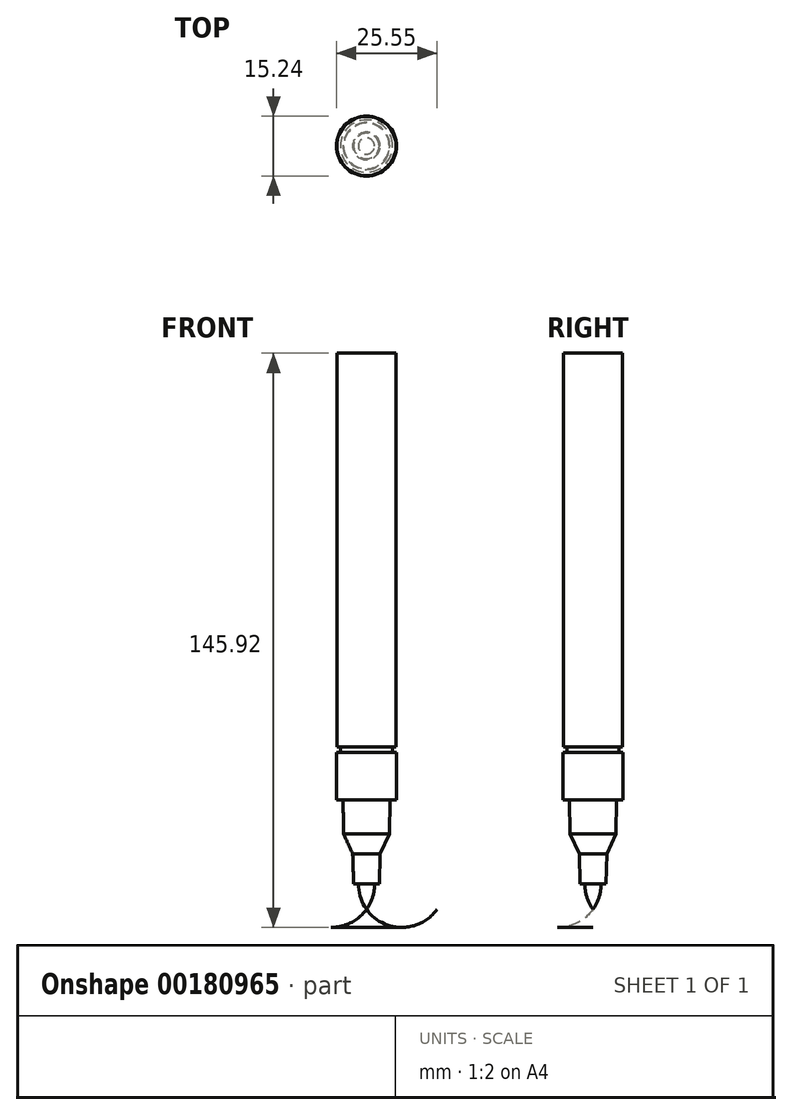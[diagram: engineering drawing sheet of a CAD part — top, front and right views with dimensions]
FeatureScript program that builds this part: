
annotation { "Feature Type Name" : "Feature", "Feature Type Description" : "" }
export const myFeature = defineFeature(function(context is Context, id is Id, definition is map)
    precondition{}
    {
        {
            var Q0;
            Q0=qCreatedBy(makeId("Top.planeOp"),FACE);
            var sketch = newSketch(context, id + "F0", { "sketchPlane" : qUnion([Q0])});
            skCircle(sketch, "E0", {"center": v(0, 0) * mm, "radius": 7.5 * mm});
            skSolve(sketch);
        }
        {
            var Q0;
            Q0=qSketchRegion(id+"F0",true);
            extrude(context, id + "F1", {"entities" : qUnion([Q0]), "depth" : 100 * mm});
        }
        {
            var Q0;
            Q0=makeQuery(id+"F1.opExtrude","CAP_FACE",FACE,{"disambiguationData":[OSD([sQuery(id+"F0.wireOp",EDGE,"E0")])],"isStart":true});
            var sketch = newSketch(context, id + "F2", { "sketchPlane" : qUnion([Q0])});
            skCircle(sketch, "E1", {"center": v(0, 0) * mm, "radius": 6.65 * mm});
            skSolve(sketch);
        }
        {
            var Q0;
            Q0=qSketchRegion(id+"F2",true);
            extrude(context, id + "F3", {"entities" : qUnion([Q0]), "operationType" : NewBodyOperationType.ADD, "depth" : 1.5 * mm});
        }
        {
            var Q0;
            Q0=makeQuery(id+"F3.opExtrude","CAP_FACE",FACE,{"disambiguationData":[OSD([sQuery(id+"F2.wireOp",EDGE,"E1")])],"isStart":false});
            var sketch = newSketch(context, id + "F4", { "sketchPlane" : qUnion([Q0])});
            skCircle(sketch, "E2", {"center": v(0, 0) * mm, "radius": 7.62 * mm});
            skSolve(sketch);
        }
        {
            var Q0;
            Q0=qSketchRegion(id+"F4",true);
            extrude(context, id + "F5", {"entities" : qUnion([Q0]), "operationType" : NewBodyOperationType.ADD, "depth" : 12 * mm});
        }
        {
            var Q0;
            Q0=makeQuery(id+"F5.opExtrude","CAP_FACE",FACE,{"disambiguationData":[OSD([sQuery(id+"F4.wireOp",EDGE,"E2")])],"isStart":false});
            var sketch = newSketch(context, id + "F6", { "sketchPlane" : qUnion([Q0])});
            skCircle(sketch, "E3", {"center": v(0, 0) * mm, "radius": 5.95 * mm});
            skSolve(sketch);
        }
        {
            var Q0;
            Q0=makeQuery(id+"F6.imprint","IMPRINT",FACE,{"disambiguationData":[TD([[makeQuery(id+"F6.imprint","IMPRINT",EDGE,{"derivedFrom":sQuery(id+"F6.wireOp",EDGE,"E3")}),1.0]])]});
            cPlane(context, id + "F7", {"entities" : qUnion([Q0]), "cplaneType" : CPlaneType.OFFSET, "offset" : 8.7 * mm, "width" : 150 * mm, "height" : 150 * mm});
        }
        {
            var Q0;
            Q0=qCreatedBy(id+"F7.planeOp",FACE);
            var sketch = newSketch(context, id + "F8", { "sketchPlane" : qUnion([Q0])});
            skCircle(sketch, "E4", {"center": v(0, 0) * mm, "radius": 5.8 * mm});
            skSolve(sketch);
        }
        {
            var Q1;
            Q1=makeQuery(id+"F6.imprint","IMPRINT",FACE,{"disambiguationData":[TD([[makeQuery(id+"F6.imprint","IMPRINT",EDGE,{"derivedFrom":sQuery(id+"F6.wireOp",EDGE,"E3")}),1.0]])]});
            var Q2;
            Q2=makeQuery(id+"F8.imprint","IMPRINT",FACE,{"disambiguationData":[TD([[makeQuery(id+"F8.imprint","IMPRINT",EDGE,{"derivedFrom":sQuery(id+"F8.wireOp",EDGE,"E4")}),1.0]])]});
            loft(context, id + "F9", {"operationType" : NewBodyOperationType.ADD, "sheetProfilesArray" : [{ "sheetProfileEntities" : qUnion([Q1]) }, { "sheetProfileEntities" : qUnion([Q2]) }]});
        }
        {
            var Q0;
            Q0=qCreatedBy(id+"F7.planeOp",FACE);
            cPlane(context, id + "F10", {"entities" : qUnion([Q0]), "cplaneType" : CPlaneType.OFFSET, "offset" : 5 * mm, "width" : 150 * mm, "height" : 150 * mm});
        }
        {
            var Q0;
            Q0=qCreatedBy(id+"F10.planeOp",FACE);
            var sketch = newSketch(context, id + "F11", { "sketchPlane" : qUnion([Q0])});
            skCircle(sketch, "E5", {"center": v(0, 0) * mm, "radius": 3.5 * mm});
            skSolve(sketch);
        }
        {
            var Q1;
            Q1=makeQuery(id+"F9.opLoft","CAP_FACE",FACE,{"disambiguationData":[OSD([makeQuery(id+"F8.imprint","IMPRINT",FACE,{"disambiguationData":[TD([[makeQuery(id+"F8.imprint","IMPRINT",EDGE,{"derivedFrom":sQuery(id+"F8.wireOp",EDGE,"E4")}),1.0]])]})])],"isStart":true});
            var Q2;
            Q2=makeQuery(id+"F11.imprint","IMPRINT",FACE,{"disambiguationData":[TD([[makeQuery(id+"F11.imprint","IMPRINT",EDGE,{"derivedFrom":sQuery(id+"F11.wireOp",EDGE,"E5")}),1.0]])]});
            loft(context, id + "F12", {"operationType" : NewBodyOperationType.ADD, "sheetProfilesArray" : [{ "sheetProfileEntities" : qUnion([Q1]) }, { "sheetProfileEntities" : qUnion([Q2]) }]});
        }
        {
            var Q0;
            Q0=qCreatedBy(id+"F10.planeOp",FACE);
            cPlane(context, id + "F13", {"entities" : qUnion([Q0]), "cplaneType" : CPlaneType.OFFSET, "offset" : 7.7 * mm, "width" : 150 * mm, "height" : 150 * mm});
        }
        {
            var Q0;
            Q0=qCreatedBy(id+"F13.planeOp",FACE);
            var sketch = newSketch(context, id + "F14", { "sketchPlane" : qUnion([Q0])});
            skCircle(sketch, "E6", {"center": v(0, 0) * mm, "radius": 3.25 * mm});
            skSolve(sketch);
        }
        {
            var Q1;
            Q1=makeQuery(id+"F12.opLoft","CAP_FACE",FACE,{"disambiguationData":[OSD([makeQuery(id+"F11.imprint","IMPRINT",FACE,{"disambiguationData":[TD([[makeQuery(id+"F11.imprint","IMPRINT",EDGE,{"derivedFrom":sQuery(id+"F11.wireOp",EDGE,"E5")}),1.0]])]})])],"isStart":true});
            var Q2;
            Q2=makeQuery(id+"F14.imprint","IMPRINT",FACE,{"disambiguationData":[TD([[makeQuery(id+"F14.imprint","IMPRINT",EDGE,{"derivedFrom":sQuery(id+"F14.wireOp",EDGE,"E6")}),1.0]])]});
            loft(context, id + "F15", {"operationType" : NewBodyOperationType.ADD, "sheetProfilesArray" : [{ "sheetProfileEntities" : qUnion([Q1]) }, { "sheetProfileEntities" : qUnion([Q2]) }]});
        }
        {
            var Q0;
            Q0=qCreatedBy(makeId("Right.planeOp"),FACE);
            var sketch = newSketch(context, id + "F16", { "sketchPlane" : qUnion([Q0])});
            skArc(sketch, "E7", {"start": v(-2.05, -34.9) * mm, "mid": v(-1.52, -38.26) * mm, "end": v(0, -41.3) * mm});
            skLineSegment(sketch, "E8", {"start": v(0, -34.9) * mm, "end": v(0, -41.3) * mm});
            skLineSegment(sketch, "E9", {"start": v(-2.05, -34.9) * mm, "end": v(-2.05, -37.03) * mm, "construction": true});
            skLineSegment(sketch, "E10", {"start": v(-2.05, -34.9) * mm, "end": v(0, -34.9) * mm});
            skSolve(sketch);
        }
        {
            var Q0;
            Q0=makeQuery(id+"F16.imprint","IMPRINT",FACE,{"disambiguationData":[TD([[makeQuery(id+"F16.imprint","IMPRINT",EDGE,{"derivedFrom":sQuery(id+"F16.wireOp",EDGE,"E7")}),1.0]])]});
            var Q1;
            Q1=sQuery(id+"F16.wireOp",EDGE,"E8");
            revolve(context, id + "F17", {"operationType" : NewBodyOperationType.ADD, "entities" : qUnion([Q0]), "axis" : qUnion([Q1]), "revolveType" : RevolveType.FULL});
        }
    });
